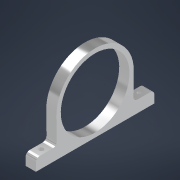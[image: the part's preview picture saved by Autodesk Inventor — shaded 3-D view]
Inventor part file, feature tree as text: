
AUTODESK INVENTOR PART (.ipt)
format: ipt  version: 2022 (Build 260153000, 153)  size: 150,016 bytes
history: native  units: in
note: dims shown in document units (in); Inventor stores cm internally (conversion verified against a paired STEP export)
features: extrude x2, sketch x2, other x1, fillet x1
ambient origin geometry x8: Origin, YZ Plane, XZ Plane, XY Plane, X Axis, Y Axis, Z Axis, Center Point
bodies: Body1 (feature_tree)
feature tree (6):
  other  "Sólido1"
  extrude  "Extrusión1"  Depth=5.9055in
  fillet  "Empalme1"  Radius=5.9055in
  extrude  "Extrusión2"  Depth=0.5118in TaperAngle=0.0deg
  sketch  "Boceto1"  dims[d0=3.4252in d2=3.8583in d3=5.9055in]
  sketch  "Boceto2"  dims[d4=0.5906in d5=0.5118in d6=0.0in d7=0.1969in d8=0.2362in d9=0.1732in d10=0.2559in d11=0.5118in d12=0.5118in d13=0.2559in d14=0.0in d15=0.0in]
